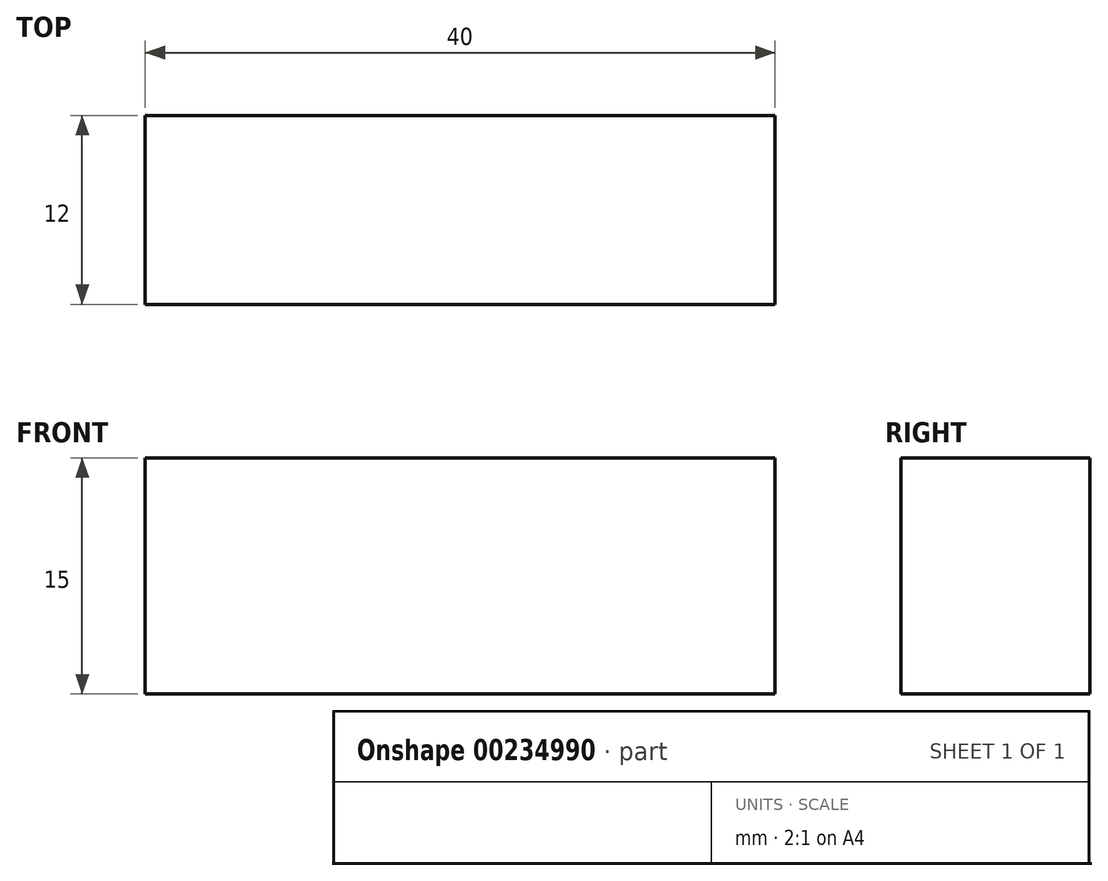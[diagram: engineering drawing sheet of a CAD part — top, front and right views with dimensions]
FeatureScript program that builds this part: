
annotation { "Feature Type Name" : "Feature", "Feature Type Description" : "" }
export const myFeature = defineFeature(function(context is Context, id is Id, definition is map)
    precondition{}
    {
        {
            var Q0;
            Q0=qCreatedBy(makeId("Front.planeOp"),FACE);
            var sketch = newSketch(context, id + "F0", { "sketchPlane" : qUnion([Q0])});
            skLineSegment(sketch, "E0.bottom", {"start": v(20, -7.5) * mm, "end": v(-20, -7.5) * mm});
            skLineSegment(sketch, "E0.top", {"start": v(20, 7.5) * mm, "end": v(-20, 7.5) * mm});
            skLineSegment(sketch, "E0.left", {"start": v(20, -7.5) * mm, "end": v(20, 7.5) * mm});
            skLineSegment(sketch, "E0.right", {"start": v(-20, -7.5) * mm, "end": v(-20, 7.5) * mm});
            skPoint(sketch, "E0.middle", {"position": v(0, 0) * mm});
            skSolve(sketch);
        }
        {
            var Q0;
            Q0=qSketchRegion(id+"F0",true);
            extrude(context, id + "F1", {"entities" : qUnion([Q0]), "endBound" : BoundingType.SYMMETRIC, "depth" : 12 * mm});
        }
    });
